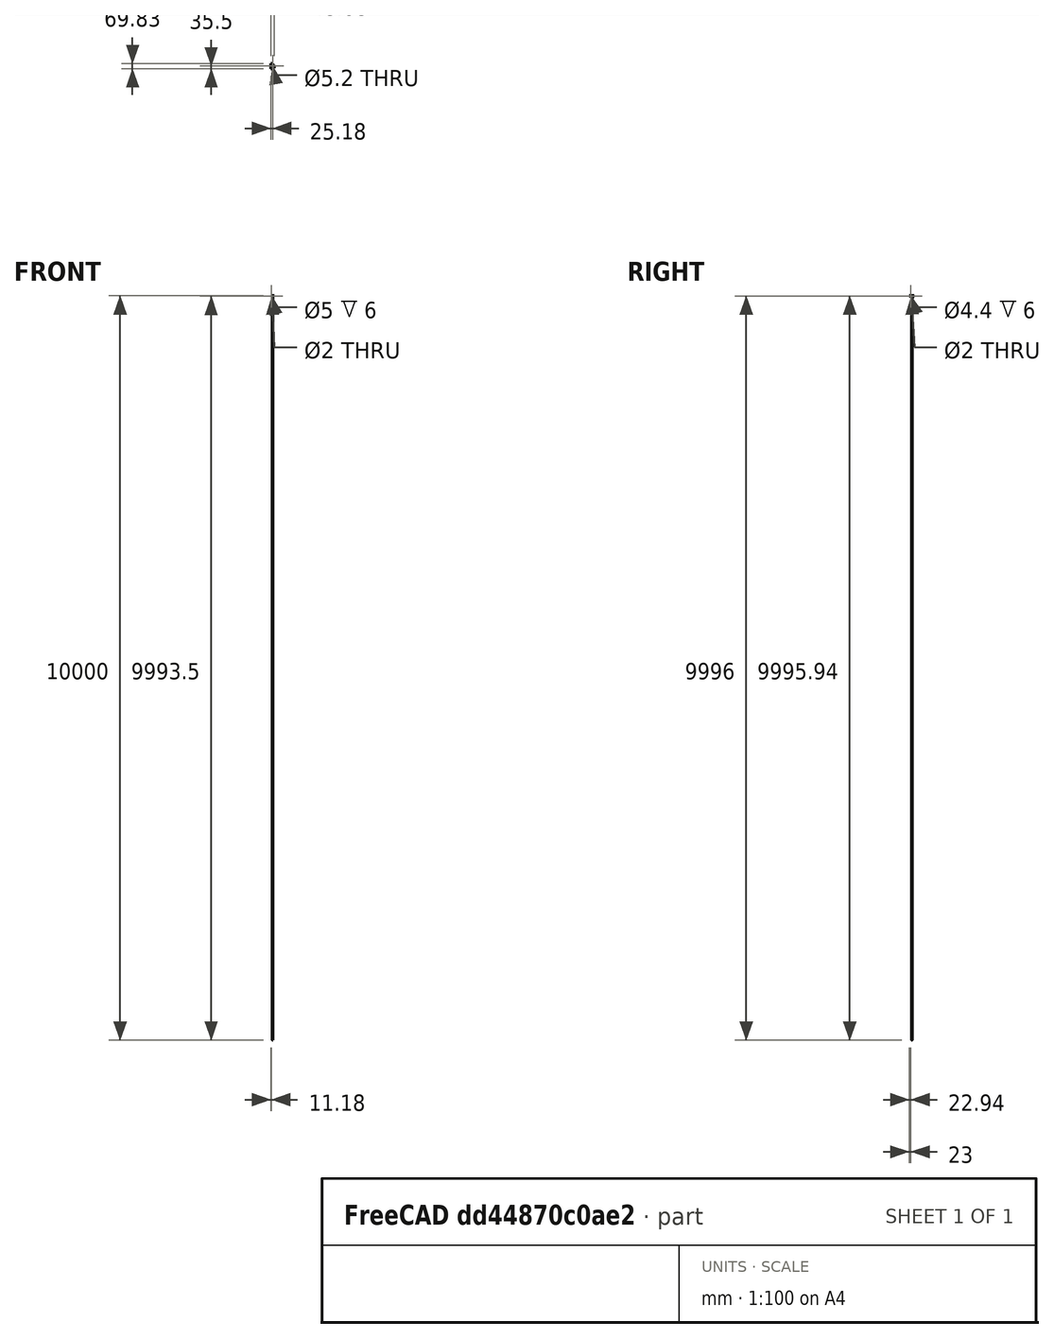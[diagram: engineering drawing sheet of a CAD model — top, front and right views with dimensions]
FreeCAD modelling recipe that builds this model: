
FCSTD DOCUMENT  (FreeCAD 0.16R)
Label: hackpan01B
License: All rights reserved
LicenseURL: http://en.wikipedia.org/wiki/All_rights_reserved
objects: Sketcher::SketchObject×8, PartDesign::Pocket×7, PartDesign::Fillet×6, PartDesign::Pad×1, PartDesign::Chamfer×1, Mesh::Feature×1
note: 31 computed .brp shape members not serialized (recipe doc carries the construction recipe); baked Part::Feature solids carry a one-line shape summary decoded from their .brp

FEATURE [Sketcher::SketchObject] Sketch
  sketch-geometry (7):
    g0: LineSegment StartX=0 StartY=50 StartZ=0 EndX=15 EndY=50 EndZ=0
    g1: LineSegment StartX=15 StartY=50 StartZ=0 EndX=15 EndY=48 EndZ=0
    g2: LineSegment StartX=15 StartY=48 StartZ=0 EndX=43 EndY=15 EndZ=0
    g3: LineSegment StartX=43 StartY=15 StartZ=0 EndX=45 EndY=15 EndZ=0
    g4: LineSegment StartX=45 StartY=15 StartZ=0 EndX=45 EndY=0 EndZ=0
    g5: LineSegment StartX=45 StartY=0 StartZ=0 EndX=0 EndY=0 EndZ=0
    g6: LineSegment StartX=0 StartY=0 StartZ=0 EndX=0 EndY=50 EndZ=0
  constraints (20):
    c: Horizontal(g0)
    c: Coincident(g0,g1)
    c: Vertical(g1)
    c: Coincident(g1,g2)
    c: Coincident(g2,g3)
    c: Horizontal(g3)
    c: Coincident(g3,g4)
    c: Vertical(g4)
    c: Coincident(g4,g5)
    c: Horizontal(g5)
    c: Coincident(g5,g6)
    c: Coincident(g6,g0)
    c: Vertical(g6)
    c: Distance(g0) = 15
    c: Distance(g4) = 15
    c: Distance(g1) = 2
    c: Distance(g3) = 2
    c: Coincident(g5,g-1)
    c: Distance(g5) = 45
    c: Distance(g6) = 50
FEATURE [PartDesign::Pad] Pad
  Length = 13
  Length2 = 100
  Sketch = -> Sketch
  Type = 0
FEATURE [Sketcher::SketchObject] Sketch001
  Placement = pos=(0,0,13) rot=(0,0,1;0rad)
  Support = -> Pad [Face9]
  sketch-geometry (1):
    g0: Circle CenterX=21.5 CenterY=22.5 CenterZ=0 NormalX=0 NormalY=0 NormalZ=1 Radius=18
  constraints (3):
    c: Radius(g0) = 18
    c: DistanceY(g0) = 22.5
    c: DistanceX(g0) = 21.5
FEATURE [PartDesign::Pocket] Pocket
  Length = 9
  Sketch = -> Sketch001
  Type = 0
FEATURE [Sketcher::SketchObject] Sketch002
  Placement = pos=(0,0,13) rot=(0,0,1;0rad)
  Support = -> Pocket [Face5]
  sketch-geometry (4):
    g0: LineSegment StartX=-3.67996 StartY=56.8256 StartZ=0 EndX=24.9554 EndY=56.8256 EndZ=0
    g1: LineSegment StartX=24.9554 StartY=56.8256 StartZ=0 EndX=24.9554 EndY=-13.0041 EndZ=0
    g2: LineSegment StartX=24.9554 StartY=-13.0041 StartZ=0 EndX=-3.67996 EndY=-13.0041 EndZ=0
    g3: LineSegment StartX=-3.67996 StartY=-13.0041 StartZ=0 EndX=-3.67996 EndY=56.8256 EndZ=0
  constraints (8):
    c: Coincident(g0,g1)
    c: Coincident(g1,g2)
    c: Coincident(g2,g3)
    c: Coincident(g3,g0)
    c: Horizontal(g0)
    c: Horizontal(g2)
    c: Vertical(g1)
    c: Vertical(g3)
FEATURE [PartDesign::Pocket] Pocket001
  Length = 1
  Sketch = -> Sketch002
  Type = 0
FEATURE [Sketcher::SketchObject] Sketch003
  ExternalGeometry = -> [Pocket001]
  Placement = pos=(0,50,0) rot=(0,0.707107,0.707107;3.14159rad)
  Support = -> Pocket001 [Face1]
  sketch-geometry (1):
    g0: Circle CenterX=-7.5 CenterY=6.5 CenterZ=0 NormalX=0 NormalY=0 NormalZ=1 Radius=2.5
  constraints (3):
    c: Radius(g0) = 2.5
    c: DistanceX(g0) = -7.5
    c: DistanceY(g0) = 6.5
FEATURE [PartDesign::Pocket] Pocket002
  Length = 6
  Sketch = -> Sketch003
  Type = 0
FEATURE [Sketcher::SketchObject] Sketch004
  ExternalGeometry = -> [Pocket002]
  Placement = pos=(0,50,0) rot=(0,0.707107,0.707107;3.14159rad)
  Support = -> Pocket002 [Face1]
  sketch-geometry (1):
    g0: Circle CenterX=-7.5 CenterY=6.5 CenterZ=0 NormalX=0 NormalY=0 NormalZ=1 Radius=1
  constraints (2):
    c: Radius(g0) = 1
    c: Coincident(g-3,g0)
FEATURE [PartDesign::Pocket] Pocket003
  Length = 19
  Sketch = -> Sketch004
  Type = 0
FEATURE [Sketcher::SketchObject] Sketch008
  Placement = pos=(0,0,13) rot=(0,0,1;0rad)
  Support = -> Pocket003 [Face14]
  sketch-geometry (1):
    g0: Circle CenterX=21.5 CenterY=22.5 CenterZ=0 NormalX=0 NormalY=0 NormalZ=1 Radius=2.6
  constraints (1):
    c: Radius(g0) = 2.6
FEATURE [PartDesign::Pocket] Pocket004
  Length = 5
  Sketch = -> Sketch008
  Type = 1
FEATURE [Sketcher::SketchObject] Sketch005
  Placement = pos=(45,0,0) rot=(0.57735,0.57735,0.57735;2.0944rad)
  Support = -> Pocket004 [Face9]
  sketch-geometry (1):
    g0: Circle CenterX=10 CenterY=9 CenterZ=0 NormalX=0 NormalY=0 NormalZ=1 Radius=2.2
  constraints (3):
    c: Radius(g0) = 2.2
    c: DistanceY(g0) = 9
    c: DistanceX(g0) = 10
FEATURE [PartDesign::Pocket] Pocket005
  Length = 6
  Sketch = -> Sketch005
  Type = 0
FEATURE [Sketcher::SketchObject] Sketch007
  Placement = pos=(45,0,0) rot=(0.57735,0.57735,0.57735;2.0944rad)
  Support = -> Pocket005 [Face9]
  sketch-geometry (1):
    g0: Circle CenterX=9.93975 CenterY=8.94018 CenterZ=0 NormalX=0 NormalY=0 NormalZ=1 Radius=1
  constraints (1):
    c: Radius(g0) = 1
FEATURE [PartDesign::Pocket] Pocket006
  Length = 19
  Sketch = -> Sketch007
  Type = 0
FEATURE [PartDesign::Fillet] Fillet
  Base = -> Pocket006 [Edge14,Edge25]
  Radius = 7
FEATURE [PartDesign::Fillet] Fillet001
  Base = -> Fillet [Edge12]
  Radius = 4
FEATURE [PartDesign::Fillet] Fillet002
  Base = -> Fillet001 [Edge36,Edge19,Edge34,Edge32]
  Radius = 1.5
FEATURE [PartDesign::Fillet] Fillet003
  Base = -> Fillet002 [Edge41,Edge63]
  Radius = 1
FEATURE [PartDesign::Fillet] Fillet004
  Base = -> Fillet003 [Edge55]
  Radius = 1
FEATURE [PartDesign::Fillet] Fillet005
  Base = -> Fillet004 [Edge9]
  Radius = 1
FEATURE [PartDesign::Chamfer] Chamfer
  Base = -> Fillet005 [Edge76,Edge74,Edge72,Edge70,Edge68,Edge64,Edge66,Edge62,Edge52,Edge60,Edge55,Edge57,Edge79]
  Size = 1
FEATURE [Mesh::Feature] Mesh  label="Chamfer (Meshed)"
